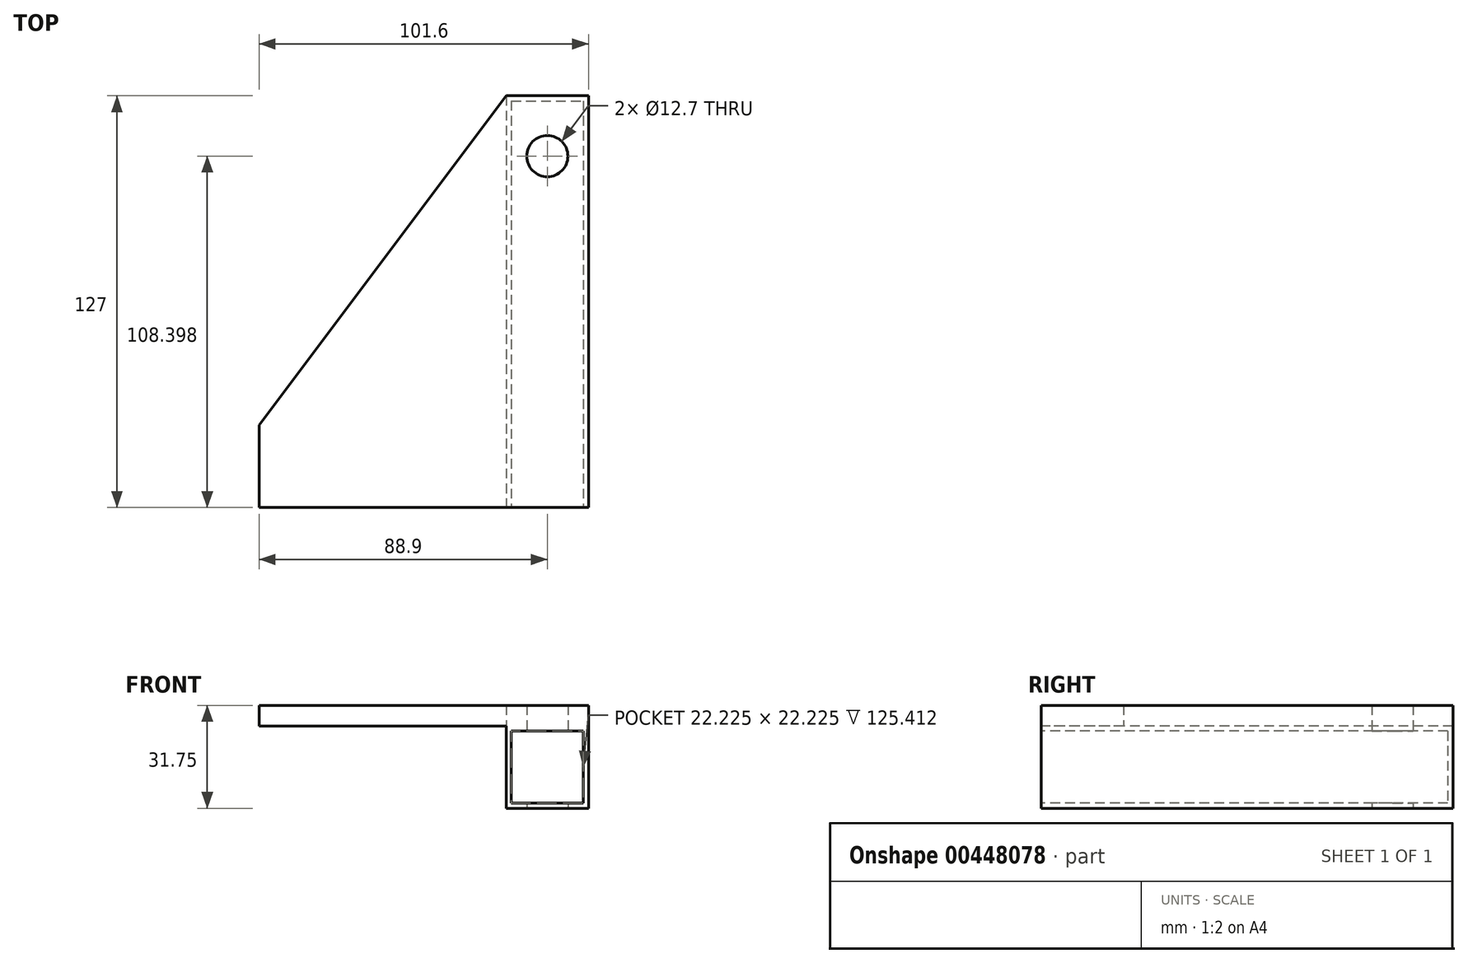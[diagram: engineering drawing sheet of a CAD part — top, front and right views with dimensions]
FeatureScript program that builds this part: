
annotation { "Feature Type Name" : "Feature", "Feature Type Description" : "" }
export const myFeature = defineFeature(function(context is Context, id is Id, definition is map)
    precondition{}
    {
        {
            var Q0;
            Q0=qCreatedBy(makeId("Top.planeOp"),FACE);
            var sketch = newSketch(context, id + "F0", { "sketchPlane" : qUnion([Q0])});
            skLineSegment(sketch, "E0.bottom", {"start": v(-12.7, 63.5) * mm, "end": v(12.7, 63.5) * mm});
            skLineSegment(sketch, "E0.top", {"start": v(-12.7, -63.5) * mm, "end": v(12.7, -63.5) * mm});
            skLineSegment(sketch, "E0.left", {"start": v(-12.7, 63.5) * mm, "end": v(-12.7, -63.5) * mm});
            skLineSegment(sketch, "E0.right", {"start": v(12.7, 63.5) * mm, "end": v(12.7, -63.5) * mm});
            skPoint(sketch, "E0.middle", {"position": v(0, 0) * mm});
            skSolve(sketch);
        }
        {
            var Q0;
            Q0=qSketchRegion(id+"F0",true);
            extrude(context, id + "F1", {"entities" : qUnion([Q0]), "depth" : 25.4 * mm});
        }
        {
            var Q0;
            Q0=makeQuery(id+"F1.opExtrude","SWEPT_FACE",FACE,{"disambiguationData":[OSD([sQuery(id+"F0.wireOp",EDGE,"E0.top")])]});
            shell(context, id + "F2", {"entities" : qUnion([Q0]), "thickness" : 1.59 * mm});
        }
        {
            var Q0;
            Q0=makeQuery(id+"F1.opExtrude","CAP_FACE",FACE,{"disambiguationData":[OSD([sQuery(id+"F0.wireOp",EDGE,"E0.bottom"),sQuery(id+"F0.wireOp",EDGE,"E0.top"),sQuery(id+"F0.wireOp",EDGE,"E0.left"),sQuery(id+"F0.wireOp",EDGE,"E0.right")])],"isStart":false});
            var sketch = newSketch(context, id + "F3", { "sketchPlane" : qUnion([Q0])});
            skLineSegment(sketch, "E1.bottom", {"start": v(-12.7, 63.5) * mm, "end": v(12.7, 63.5) * mm});
            skLineSegment(sketch, "E1.top", {"start": v(-12.7, -63.5) * mm, "end": v(12.7, -63.5) * mm});
            skLineSegment(sketch, "E1.left", {"start": v(-12.7, 63.5) * mm, "end": v(-12.7, -63.5) * mm});
            skLineSegment(sketch, "E1.right", {"start": v(12.7, 63.5) * mm, "end": v(12.7, -63.5) * mm});
            skLineSegment(sketch, "E2.bottom", {"start": v(12.7, 63.5) * mm, "end": v(88.9, 63.5) * mm});
            skLineSegment(sketch, "E2.top", {"start": v(12.7, -63.5) * mm, "end": v(88.9, -63.5) * mm});
            skLineSegment(sketch, "E2.right", {"start": v(88.9, 63.5) * mm, "end": v(88.9, -63.5) * mm});
            skLineSegment(sketch, "E3", {"start": v(12.7, 63.5) * mm, "end": v(88.9, -38.1) * mm});
            skLineSegment(sketch, "E4.bottom", {"start": v(-12.7, 63.5) * mm, "end": v(-88.9, 63.5) * mm});
            skLineSegment(sketch, "E4.top", {"start": v(-12.7, -63.5) * mm, "end": v(-88.9, -63.5) * mm});
            skLineSegment(sketch, "E4.right", {"start": v(-88.9, 63.5) * mm, "end": v(-88.9, -63.5) * mm});
            skLineSegment(sketch, "E5", {"start": v(-12.7, 63.5) * mm, "end": v(-88.9, -38.1) * mm});
            skSolve(sketch);
        }
        {
            var Q0;
            Q0=makeQuery(id+"F3.imprint","IMPRINT",FACE,{"disambiguationData":[TD([[makeQuery(id+"F3.imprint","IMPRINT",EDGE,{"derivedFrom":sQuery(id+"F3.wireOp",EDGE,"E1.bottom")}),-1.0]])]});
            var Q1;
            {var subQ0=sQuery(id+"F3.wireOp",EDGE,"E4.top");Q1=makeQuery(id+"F3.imprint","IMPRINT",FACE,{"disambiguationData":[TD([[makeQuery(id+"F3.imprint","IMPRINT",EDGE,{"derivedFrom":subQ0}),-1.0]])]});}
            extrude(context, id + "F4", {"entities" : qUnion([Q0, Q1]), "operationType" : NewBodyOperationType.ADD, "depth" : 6.35 * mm});
        }
        {
            var Q0;
            Q0=makeQuery(id+"F1.opExtrude","CAP_FACE",FACE,{"disambiguationData":[OSD([sQuery(id+"F0.wireOp",EDGE,"E0.bottom"),sQuery(id+"F0.wireOp",EDGE,"E0.top"),sQuery(id+"F0.wireOp",EDGE,"E0.left"),sQuery(id+"F0.wireOp",EDGE,"E0.right")])],"isStart":true});
            var sketch = newSketch(context, id + "F5", { "sketchPlane" : qUnion([Q0])});
            skCircle(sketch, "E6", {"center": v(0, -44.9) * mm, "radius": 6.35 * mm});
            skPoint(sketch, "E6.centerSnap0", {"position": v(0, -63.5) * mm});
            skSolve(sketch);
        }
        {
            var Q0;
            Q0=qSketchRegion(id+"F5",true);
            extrude(context, id + "F6", {"entities" : qUnion([Q0]), "operationType" : NewBodyOperationType.REMOVE, "endBound" : BoundingType.THROUGH_ALL, "oppositeDirection" : true, "depth" : 25.4 * mm});
        }
    });
